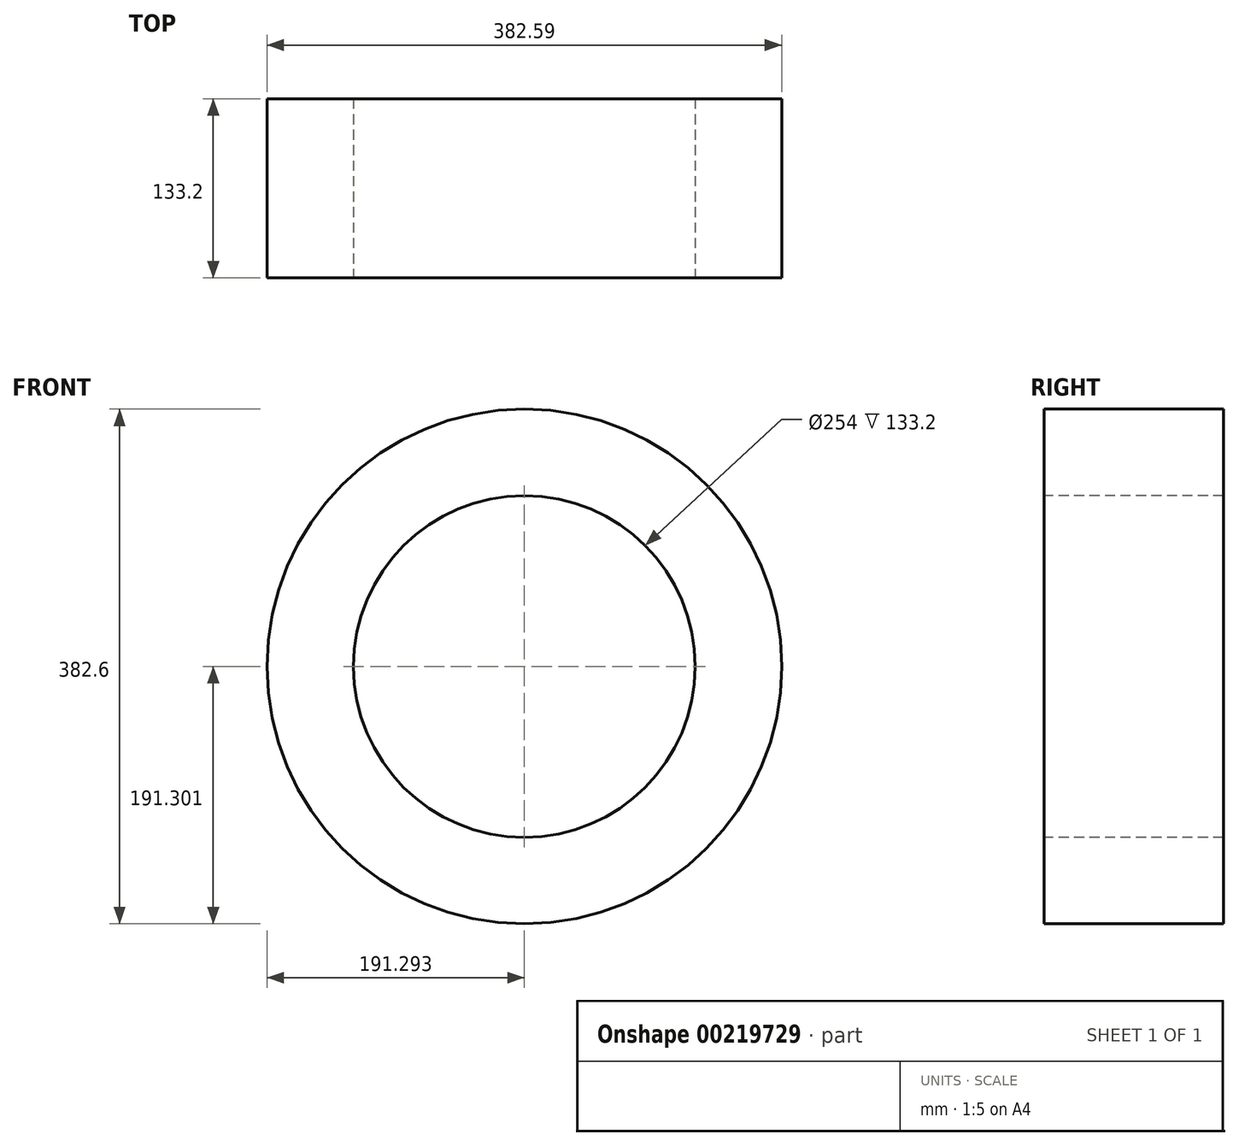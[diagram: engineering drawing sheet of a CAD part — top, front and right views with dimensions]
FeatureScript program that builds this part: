
annotation { "Feature Type Name" : "Feature", "Feature Type Description" : "" }
export const myFeature = defineFeature(function(context is Context, id is Id, definition is map)
    precondition{}
    {
        {
            var Q0;
            Q0=qCreatedBy(makeId("Front.planeOp"),FACE);
            var sketch = newSketch(context, id + "F0", { "sketchPlane" : qUnion([Q0])});
            skCircle(sketch, "E0", {"center": v(-134.23, 136.3) * mm, "radius": 191.3 * mm});
            skSolve(sketch);
        }
        {
            var Q0;
            Q0=makeQuery(id+"F0.imprint","IMPRINT",FACE,{"disambiguationData":[TD([[makeQuery(id+"F0.imprint","IMPRINT",EDGE,{"derivedFrom":sQuery(id+"F0.wireOp",EDGE,"E0")}),1.0]])]});
            extrude(context, id + "F1", {"entities" : qUnion([Q0]), "depth" : 133.2 * mm});
        }
        {
            var Q0;
            Q0=makeQuery(id+"F1.opExtrude","CAP_FACE",FACE,{"disambiguationData":[OSD([sQuery(id+"F0.wireOp",EDGE,"E0")])],"isStart":false});
            var sketch = newSketch(context, id + "F2", { "sketchPlane" : qUnion([Q0])});
            skCircle(sketch, "E1", {"center": v(-134.23, 136.3) * mm, "radius": 121.78 * mm});
            skSolve(sketch);
        }
        {
            var Q0;
            Q0=sQuery(id+"F2.wireOp",VERTEX,"E1.center");
            var Q1;
            Q1=makeQuery(id+"F1.opExtrude","SWEPT_BODY",BODY,{"disambiguationData":[OSD([sQuery(id+"F0.wireOp",EDGE,"E0")])]});
            hole(context, id + "F3", {"style" : HoleStyle.SIMPLE, "endStyle" : HoleEndStyle.THROUGH, "holeDiameter" : 254 * mm, "locations" : qUnion([Q0]), "scope" : qUnion([Q1]), "isTappedThrough" : true});
        }
    });
